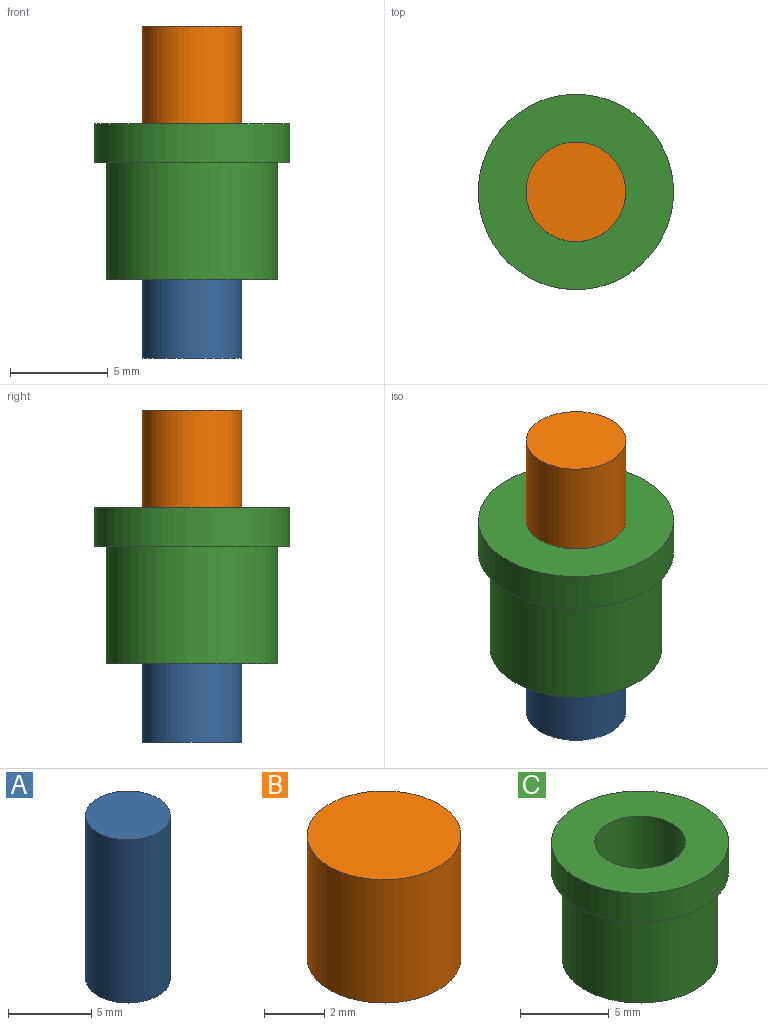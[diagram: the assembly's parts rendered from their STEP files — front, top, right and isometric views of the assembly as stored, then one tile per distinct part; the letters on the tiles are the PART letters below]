
ASSEMBLY  parts=3 mates=2
PART A: 3 faces, bbox 5.1x5.1x12 mm
  f0: cylinder r=2.55mm len=12mm, axis (0,0,1), area 192.3mm2, adj f1,f2
  f1: plane 5.1x5.1mm, normal (0,0,-1), area 20.4mm2, adj f0
  f2: plane 5.1x5.1mm, normal (0,0,1), area 20.4mm2, adj f0
PART B: 3 faces, bbox 5.1x5.1x5 mm
  f0: cylinder r=2.55mm len=5.1mm, axis (0,0,-1), area 80.1mm2, adj f1,f2
  f1: plane 5.1x5.1mm, normal (0,0,1), area 20.4mm2, adj f0
  f2: plane 5.1x5.1mm, normal (0,0,-1), area 20.4mm2, adj f0
PART C: 6 faces, bbox 10x10x8 mm
  f0: cylinder r=5mm len=10mm, axis (0,0,1), area 62.8mm2, adj f1,f2
  f1: plane 10x10mm, normal (0,0,-1), area 17.7mm2, adj f0,f3
  f2: plane 10x10mm, normal (0,0,1), area 58.1mm2, adj f0,f4
  f3: cylinder r=4.4mm len=8.8mm, axis (0,0,1), area 165.9mm2, adj f1,f5
  f4: cylinder r=2.55mm len=8mm, axis (0,0,1), area 128.2mm2, adj f2,f5
  f5: plane 8.8x8.8mm, normal (0,0,-1), area 40.4mm2, adj f3,f4
PLACE A t=(-2.08,0.06,0.43)mm
PLACE B t=(-2.08,0.06,0.43)mm
PLACE C t=(-2.08,0.06,0.43)mm
MATE fastened B.f0 <-> C.f4  axis (0,0,-1) through (-2.08,0.06,0.43)mm
MATE fastened B.f0 <-> A.f0  axis (0,0,-1) through (-2.08,0.06,0.43)mm
